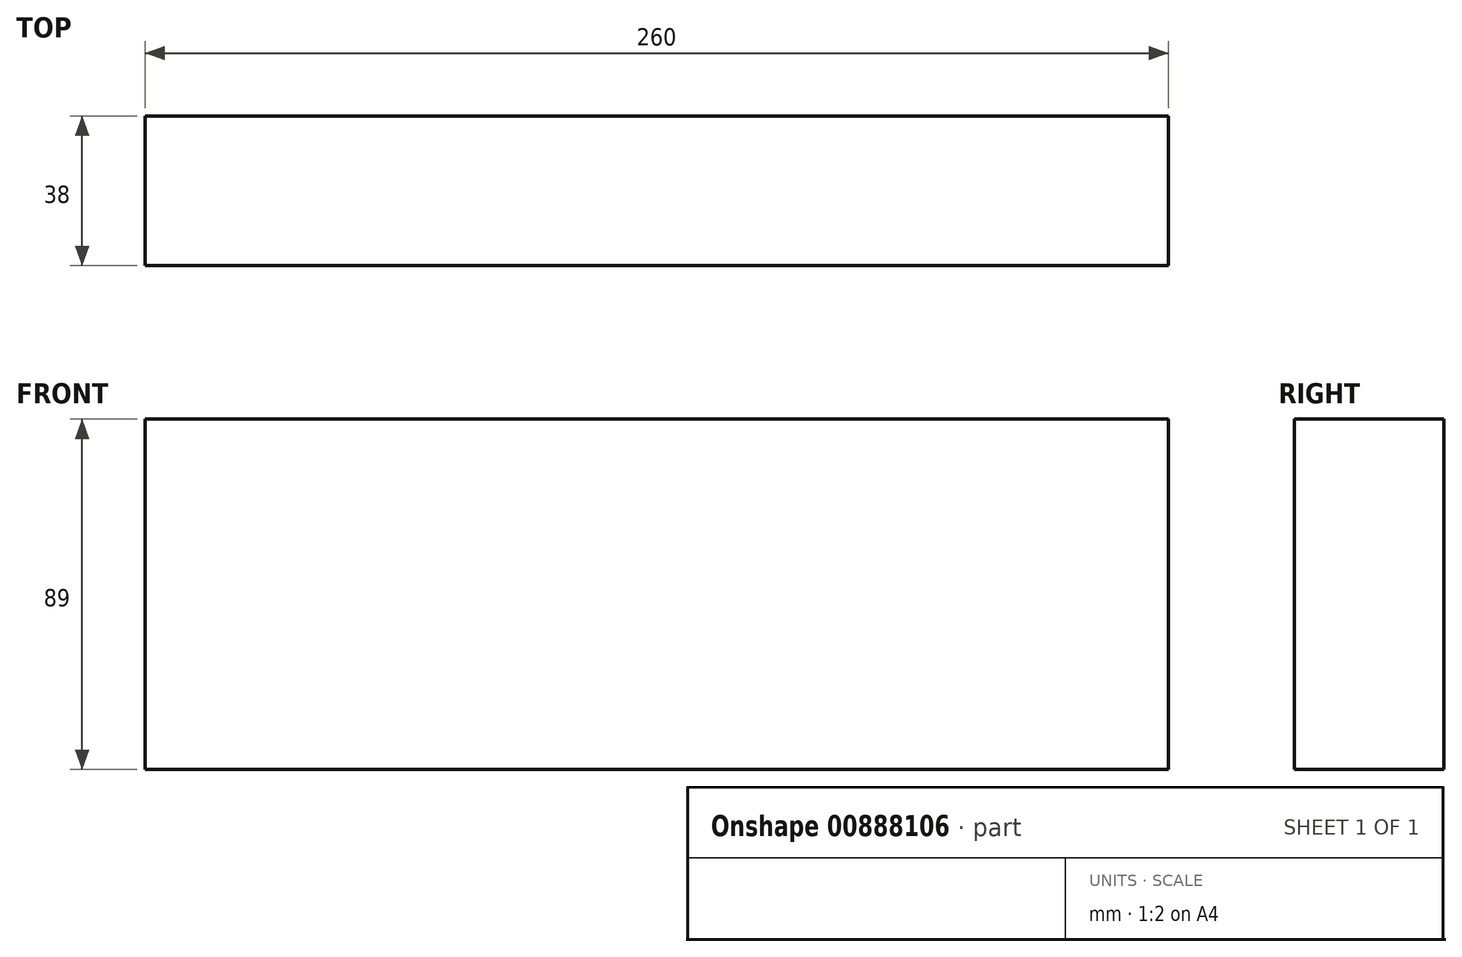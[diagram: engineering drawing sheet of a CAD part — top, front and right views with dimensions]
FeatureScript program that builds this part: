
annotation { "Feature Type Name" : "Feature", "Feature Type Description" : "" }
export const myFeature = defineFeature(function(context is Context, id is Id, definition is map)
    precondition{}
    {
        {
            var Q0;
            Q0=qCreatedBy(makeId("Front.planeOp"),FACE);
            var sketch = newSketch(context, id + "F0", { "sketchPlane" : qUnion([Q0])});
            skLineSegment(sketch, "E0.bottom", {"start": v(-206.37, 40) * mm, "end": v(53.63, 40) * mm});
            skLineSegment(sketch, "E0.top", {"start": v(-206.37, -49) * mm, "end": v(53.63, -49) * mm});
            skLineSegment(sketch, "E0.left", {"start": v(-206.37, 40) * mm, "end": v(-206.37, -49) * mm});
            skLineSegment(sketch, "E0.right", {"start": v(53.63, 40) * mm, "end": v(53.63, -49) * mm});
            skSolve(sketch);
        }
        {
            var Q0;
            Q0=makeQuery(id+"F0.imprint","IMPRINT",FACE,{"disambiguationData":[TD([[makeQuery(id+"F0.imprint","IMPRINT",EDGE,{"derivedFrom":sQuery(id+"F0.wireOp",EDGE,"E0.bottom")}),-1.0]])]});
            extrude(context, id + "F1", {"entities" : qUnion([Q0]), "depth" : 38 * mm, "offsetDistance" : 25 * mm});
        }
    });
